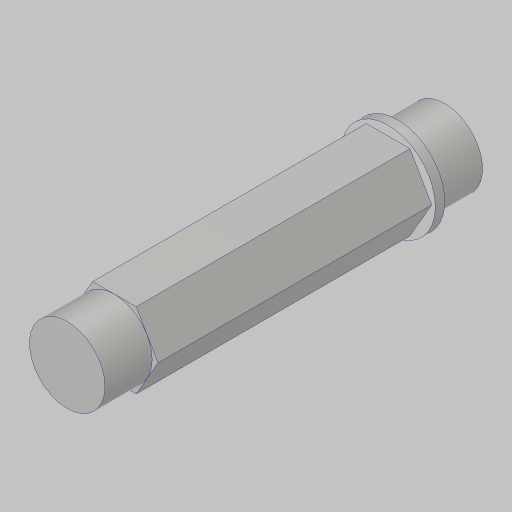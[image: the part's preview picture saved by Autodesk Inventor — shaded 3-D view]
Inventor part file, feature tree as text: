
AUTODESK INVENTOR PART (.ipt)
format: ipt  version: 2023.5 (Build 275446000, 446)  size: 147,456 bytes
history: native  units: in
note: dims shown in document units (in); Inventor stores cm internally (conversion verified against a paired STEP export)
features: extrude x5, sketch x5, projected_geometry x4
ambient origin geometry x8: Origin, YZ Plane, XZ Plane, XY Plane, X Axis, Y Axis, Z Axis, Center Point
bodies: Solid1 (feature_tree)
feature tree (14):
  extrude  "Extrusion1"  Depth=3.5625in TaperAngle=0.0deg
  extrude  "Extrusion2"  Depth=2.125in TaperAngle=0.0deg
  extrude  "Extrusion3"  Depth=0.3125in TaperAngle=0.0deg
  extrude  "Extrusion4"  TaperAngle=0.0deg  [1 undecoded]
  extrude  "Extrusion5"  Depth=0.3125in TaperAngle=0.0deg
  sketch  "Sketch1"  dims[d0=0.625in d1=3.5625in d2=0.0in]
  sketch  "Sketch2"  dims[d3=0.5in d4=2.125in d5=0.0in]
  projected_geometry  "Projected Loop1"
  sketch  "Sketch3"  dims[d6=0.5in d7=0.3125in d8=0.0in]
  projected_geometry  "Projected Loop2"
  sketch  "Sketch4"  dims[d9=2.5in d10=0.0in d11=0.0in]
  sketch  "Sketch5"  dims[d12=0.5in d13=0.3125in d14=0.0in]
  projected_geometry  "Project Cut Edges1"
  projected_geometry  "Project Cut Edges2"
note: 1 required parameter value undecoded (feature->parameter linkage not recoverable at this tier; creation-order binding heuristic only, values carry confidence <= 0.55)
